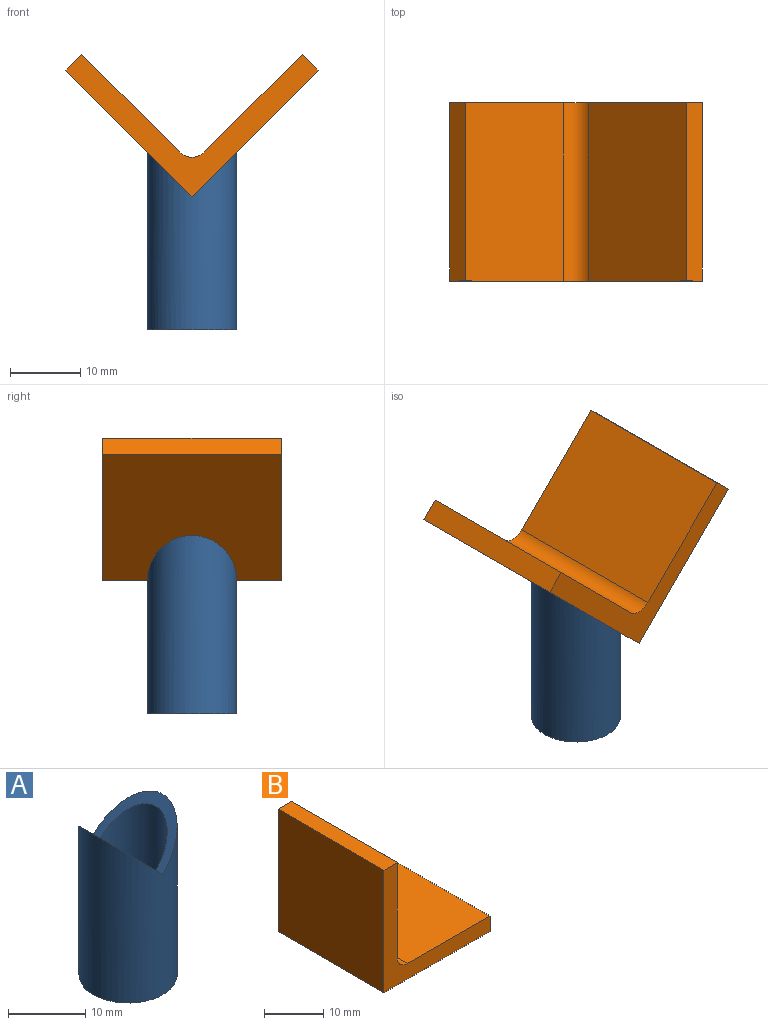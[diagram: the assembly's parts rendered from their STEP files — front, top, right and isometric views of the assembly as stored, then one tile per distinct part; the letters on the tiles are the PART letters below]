
ASSEMBLY  parts=2 mates=1
PART A: 5 faces, bbox 12.7x12.7x25.4 mm
  f0: cylinder r=5.08mm len=24.15mm, axis (0,0,-1), area 711.3mm2, adj f2,f3,f4
  f1: cylinder r=6.35mm len=25.42mm, axis (0,0,-1), area 921.4mm2, adj f2,f3,f4
  f2: plane 12.7x12.7mm, normal (0,0,-1), area 45.6mm2, adj f0,f1
  f3: plane 12.7x6.35mm, normal (0.71,0,0.71), area 32.2mm2, adj f0,f1,f4
  f4: plane 12.7x6.35mm, normal (-0.71,0,0.71), area 32.2mm2, adj f0,f1,f3
PART B: 9 faces, bbox 25.4x25.4x25.4 mm
  f0: plane 25.4x25.4mm, normal (-1,0,0), area 645.2mm2, adj f1,f5,f6,f7
  f1: plane 25.4x25.4mm, normal (0,0,-1), area 645.2mm2, adj f0,f2,f6,f7
  f2: plane 25.4x3.18mm, normal (1,0,0), area 80.6mm2, adj f1,f3,f6,f7
  f3: plane 25.4x19.69mm, normal (0,0,1), area 500mm2, adj f2,f6,f7,f8
  f4: plane 25.4x19.69mm, normal (1,0,0), area 500mm2, adj f5,f6,f7,f8
  f5: plane 25.4x3.18mm, normal (0,0,1), area 80.6mm2, adj f0,f4,f6,f7
  f6: plane 25.4x25.4mm, normal (0,-1,0), area 152.6mm2, adj f0,f1,f2,f3,f4,f5,f8
  f7: plane 25.4x25.4mm, normal (0,1,0), area 152.6mm2, adj f0,f1,f2,f3,f4,f5,f8
  f8: cylinder r=2.54mm len=25.4mm, axis (0,1,0), area 101.3mm2, adj f3,f4,f6,f7
PLACE A t=(-13.64,-1.75,-3.52)mm fixed
PLACE B rot(axis=(-0.38,0,-0.92),180deg) t=(-13.64,-14.45,15.53)mm
MATE fastened A.f4 <-> B.f0  axis (-0.71,0,0.71) through (-13.64,-1.75,15.53)mm
